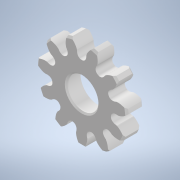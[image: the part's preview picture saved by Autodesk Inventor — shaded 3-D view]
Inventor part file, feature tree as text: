
AUTODESK INVENTOR PART (.ipt)
format: ipt  version: 2022 (Build 260153000, 153)  size: 397,824 bytes
history: native  units: mm
features: extrude x4, sketch x4, chamfer x2, other x1, pattern_circular x1
ambient origin geometry x8: Origin, YZ Plane, XZ Plane, XY Plane, X Axis, Y Axis, Z Axis, Center Point
bodies: Body1 (feature_tree)
feature tree (12):
  other  "Твердое тело1"
  extrude  "Выдавливание1"  Depth=4.75mm TaperAngle=0.0deg
  chamfer  "Фаска2"  Distance=0.5mm Angle=45.0deg
  extrude  "Выдавливание4"  Depth=4.8mm TaperAngle=0.0deg
  pattern_circular  "Круговой массив3"  Count=11 Angle=360.0deg
  extrude  "Выдавливание5"  Depth=10.2mm
  extrude  "Выдавливание6"  Depth=4.05mm TaperAngle=0.0deg
  chamfer  "Фаска3"  Distance=4.2mm
  sketch  "Эскиз1"
  sketch  "Эскиз4"
  sketch  "Эскиз5"
  sketch  "Эскиз6"
